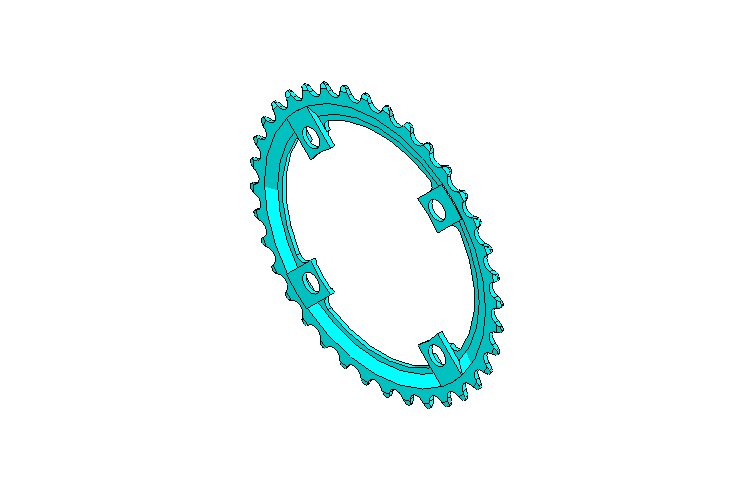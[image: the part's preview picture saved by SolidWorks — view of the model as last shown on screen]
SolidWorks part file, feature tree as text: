
SOLIDWORKS PART (.sldprt)
format: sldprt  version: not decoded by parser v0  size: 1,356,800 bytes
history: native  units: mm
features: sketch x9, cut_extrude x5, plane x3, extrude x3, pattern_circular x2, material x1, revolve x1, fillet x1 (+10 scaffold rows collapsed)
feature tree (35):
  scaffold x10  (default folders/planes/origin — collapsed)
  material  "Matériau <non spécifié>"
  plane  "Plan de face"
  plane  "Plan de dessus"
  plane  "Plan de droite"
  sketch  "Esquisse3"  dims[c1.D1=1.0mm c1.D2=2.5mm c1.D3=2.0mm c1.D4=147.5mm c1.D5=4.0mm c1.D6=112.5mm c1.D7=130.0mm c1.D8=118.5mm c1.D10=4.0mm c1.D11=1.0mm c1.D12=2.5mm c2.D2=147.5mm c2.D3=130.0mm c2.D4=118.5mm c2.D13=112.5mm c3.D3=2.0mm c3.D9=2.0mm]
  revolve  "Révolution2"  Angle=360deg
  sketch  "Esquisse2"  dims[c1.D1=8.0mm c1.D3=4.0mm c2.D1=8.0mm c2.D3=4.0mm c2.D4=1.5mm c3.D3=54.75mm c3.D2=9.5mm c4.D3=4.0mm c4.D2=~2.039916mm c5.D2=25.0deg c5.D3=2.0mm]
  cut_extrude  "Enlèv. mat.-Extru.1"  [1 undecoded]
  pattern_circular  "Répétition circulaire1"  Count=36 Angle=10deg
  sketch  "Esquisse4"  dims[c1.D3=90.0mm c1.D1=~96.665558mm c2.D1=45.0deg c2.D2=16.5mm c2.D3=~52.83244mm]
  extrude  "Extrusion1"  Depth=2mm
  sketch  "Esquisse8"  dims[D2=~3.872857mm D1=2.0mm D3=~55.901699mm]
  extrude  "Extrusion4"  Depth=2mm
  sketch  "Esquisse10"
  extrude  "Extrusion5"  [1 undecoded]
  sketch  "Esquisse11"  dims[D1=90.0mm]
  cut_extrude  "Enlèv. mat.-Extru.2"  [1 undecoded]
  sketch  "Esquisse13"
  cut_extrude  "Enlèv. mat.-Extru.3"  [1 undecoded]
  fillet  "Congé4"  Radius=2mm
  sketch  "Esquisse15"  dims[D1=14.0mm D2=~8.838835mm]
  cut_extrude  "Enlèv. mat.-Extru.5"  [1 undecoded]
  pattern_circular  "Répétition circulaire2"  Count=4 Angle=90deg
  sketch  "Esquisse14"  dims[D1=10.0mm D2=104.0mm]
  cut_extrude  "Enlèv. mat.-Extru.4"  [1 undecoded]
decode coverage: 13 of 21 modeling features carry decoded parameters
note: ~ marks probable driven/reference dimensions
note: 6 parameter values undecoded
summary: no parameter record found for 6 features
note: suppression state not decoded; provenance and decode notes live in map.json
